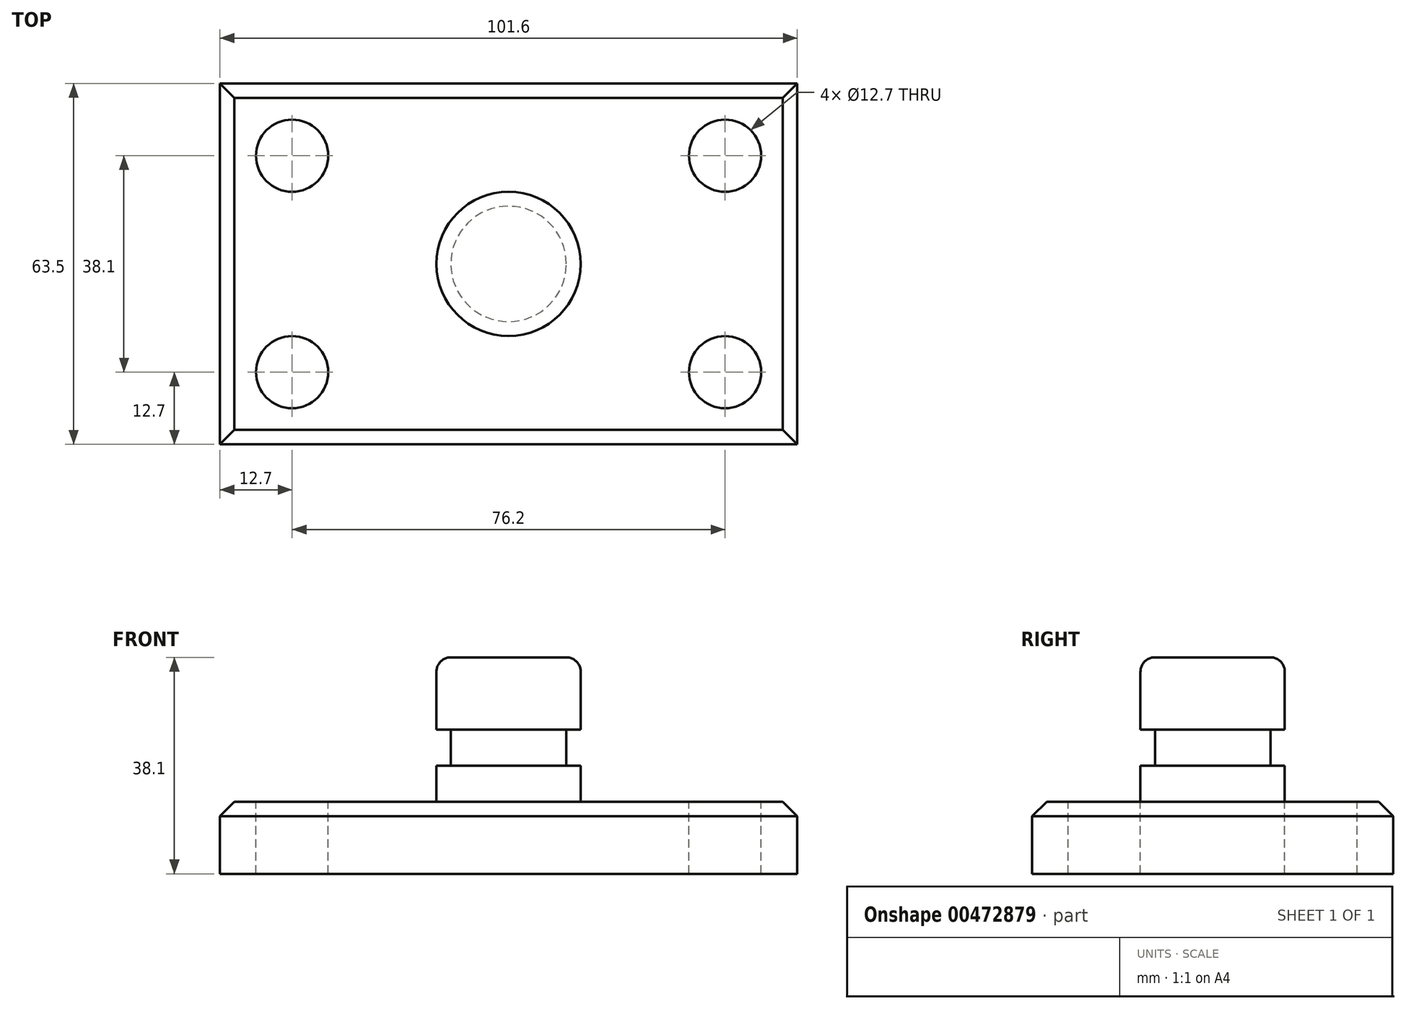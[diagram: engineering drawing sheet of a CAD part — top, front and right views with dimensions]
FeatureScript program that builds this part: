
annotation { "Feature Type Name" : "Feature", "Feature Type Description" : "" }
export const myFeature = defineFeature(function(context is Context, id is Id, definition is map)
    precondition{}
    {
        {
            var Q0;
            Q0=qCreatedBy(makeId("Top.planeOp"),FACE);
            var sketch = newSketch(context, id + "F0", { "sketchPlane" : qUnion([Q0])});
            skLineSegment(sketch, "E0.bottom", {"start": v(-50.8, -31.75) * mm, "end": v(50.8, -31.75) * mm});
            skLineSegment(sketch, "E0.top", {"start": v(-50.8, 31.75) * mm, "end": v(50.8, 31.75) * mm});
            skLineSegment(sketch, "E0.left", {"start": v(-50.8, -31.75) * mm, "end": v(-50.8, 31.75) * mm});
            skLineSegment(sketch, "E0.right", {"start": v(50.8, -31.75) * mm, "end": v(50.8, 31.75) * mm});
            skPoint(sketch, "E0.middle", {"position": v(0, 0) * mm});
            skSolve(sketch);
        }
        {
            var Q0;
            Q0=makeQuery(id+"F0.imprint","IMPRINT",FACE,{"disambiguationData":[TD([[makeQuery(id+"F0.imprint","IMPRINT",EDGE,{"derivedFrom":sQuery(id+"F0.wireOp",EDGE,"E0.bottom")}),1.0]])]});
            extrude(context, id + "F1", {"entities" : qUnion([Q0]), "depth" : 12.7 * mm});
        }
        {
            var Q0;
            Q0=makeQuery(id+"F1.opExtrude","CAP_FACE",FACE,{"disambiguationData":[OSD([sQuery(id+"F0.wireOp",EDGE,"E0.bottom"),sQuery(id+"F0.wireOp",EDGE,"E0.top"),sQuery(id+"F0.wireOp",EDGE,"E0.left"),sQuery(id+"F0.wireOp",EDGE,"E0.right")])],"isStart":false});
            var sketch = newSketch(context, id + "F2", { "sketchPlane" : qUnion([Q0])});
            skCircle(sketch, "E1", {"center": v(-38.1, 19.05) * mm, "radius": 6.35 * mm});
            skCircle(sketch, "E2", {"center": v(-38.1, -19.05) * mm, "radius": 6.35 * mm});
            skCircle(sketch, "E3", {"center": v(38.1, 19.05) * mm, "radius": 6.35 * mm});
            skCircle(sketch, "E4", {"center": v(38.1, -19.05) * mm, "radius": 6.35 * mm});
            skSolve(sketch);
        }
        {
            var Q0;
            Q0 = qSketchRegion(id + "F2", true);
            extrude(context, id + "F3", {"entities" : qUnion([Q0]), "operationType" : NewBodyOperationType.REMOVE, "endBound" : BoundingType.THROUGH_ALL, "oppositeDirection" : true, "depth" : 12.7 * mm});
        }
        {
            var Q0;
            Q0=qCreatedBy(makeId("Front.planeOp"),FACE);
            var sketch = newSketch(context, id + "F4", { "sketchPlane" : qUnion([Q0])});
            skLineSegment(sketch, "E5.bottom", {"start": v(0, 12.7) * mm, "end": v(12.7, 12.7) * mm});
            skLineSegment(sketch, "E5.top", {"start": v(0, 38.1) * mm, "end": v(12.7, 38.1) * mm});
            skLineSegment(sketch, "E5.left", {"start": v(0, 12.7) * mm, "end": v(0, 38.1) * mm});
            skLineSegment(sketch, "E5.right", {"start": v(12.7, 12.7) * mm, "end": v(12.7, 38.1) * mm});
            skSolve(sketch);
        }
        {
            var Q0;
            Q0=makeQuery(id+"F4.imprint","IMPRINT",FACE,{"disambiguationData":[TD([[makeQuery(id+"F4.imprint","IMPRINT",EDGE,{"derivedFrom":sQuery(id+"F4.wireOp",EDGE,"E5.bottom")}),1.0]])]});
            var Q1;
            Q1=sQuery(id+"F4.wireOp",EDGE,"E5.left");
            revolve(context, id + "F5", {"operationType" : NewBodyOperationType.ADD, "entities" : qUnion([Q0]), "axis" : qUnion([Q1]), "revolveType" : RevolveType.FULL});
        }
        {
            var Q0;
            Q0=qCreatedBy(makeId("Front.planeOp"),FACE);
            var sketch = newSketch(context, id + "F6", { "sketchPlane" : qUnion([Q0])});
            skLineSegment(sketch, "E6.bottom", {"start": v(10.16, 25.4) * mm, "end": v(16.51, 25.4) * mm});
            skLineSegment(sketch, "E6.top", {"start": v(10.16, 19.05) * mm, "end": v(16.51, 19.05) * mm});
            skLineSegment(sketch, "E6.left", {"start": v(10.16, 25.4) * mm, "end": v(10.16, 19.05) * mm});
            skLineSegment(sketch, "E6.right", {"start": v(16.51, 25.4) * mm, "end": v(16.51, 19.05) * mm});
            skSolve(sketch);
        }
        {
            var Q0;
            Q0=makeQuery(id+"F6.imprint","IMPRINT",FACE,{"disambiguationData":[TD([[makeQuery(id+"F6.imprint","IMPRINT",EDGE,{"derivedFrom":sQuery(id+"F6.wireOp",EDGE,"E6.bottom")}),-1.0]])]});
            var Q1;
            Q1=makeQuery(id+"F5.opRevolve","SWEPT_FACE",FACE,{"disambiguationData":[OSD([sQuery(id+"F4.wireOp",EDGE,"E5.right")])]});
            revolve(context, id + "F7", {"operationType" : NewBodyOperationType.REMOVE, "entities" : qUnion([Q0]), "axis" : qUnion([Q1]), "revolveType" : RevolveType.FULL, "oppositeDirection" : true});
        }
        {
            var Q0;
            Q0=makeQuery(id+"F5.opRevolve","SWEPT_FACE",FACE,{"disambiguationData":[OSD([sQuery(id+"F4.wireOp",EDGE,"E5.top")])]});
            var Q1;
            Q1=makeQuery(id+"F5.opRevolve","SWEPT_EDGE",EDGE,{"disambiguationData":[OSD([sQuery(id+"F4.wireOp",EDGE,"E5.bottom"),sQuery(id+"F4.wireOp",EDGE,"E5.right")])]});
            fillet(context, id + "F8", {"entities" : qUnion([Q0, Q1]), "radius" : 2.54 * mm, "tangentPropagation" : true, "allowEdgeOverflow" : false});
        }
        {
            var Q0;
            Q0=makeQuery(id+"F1.opExtrude","CAP_EDGE",EDGE,{"disambiguationData":[OSD([sQuery(id+"F0.wireOp",EDGE,"E0.top")])],"isStart":false});
            var Q1;
            Q1=makeQuery(id+"F1.opExtrude","CAP_EDGE",EDGE,{"disambiguationData":[OSD([sQuery(id+"F0.wireOp",EDGE,"E0.left")])],"isStart":false});
            var Q2;
            Q2=makeQuery(id+"F1.opExtrude","CAP_EDGE",EDGE,{"disambiguationData":[OSD([sQuery(id+"F0.wireOp",EDGE,"E0.right")])],"isStart":false});
            var Q3;
            Q3=makeQuery(id+"F1.opExtrude","CAP_EDGE",EDGE,{"disambiguationData":[OSD([sQuery(id+"F0.wireOp",EDGE,"E0.bottom")])],"isStart":false});
            chamfer(context, id + "F9", {"entities" : qUnion([Q0, Q1, Q2, Q3]), "width" : 2.54 * mm, "tangentPropagation" : true});
        }
    });
